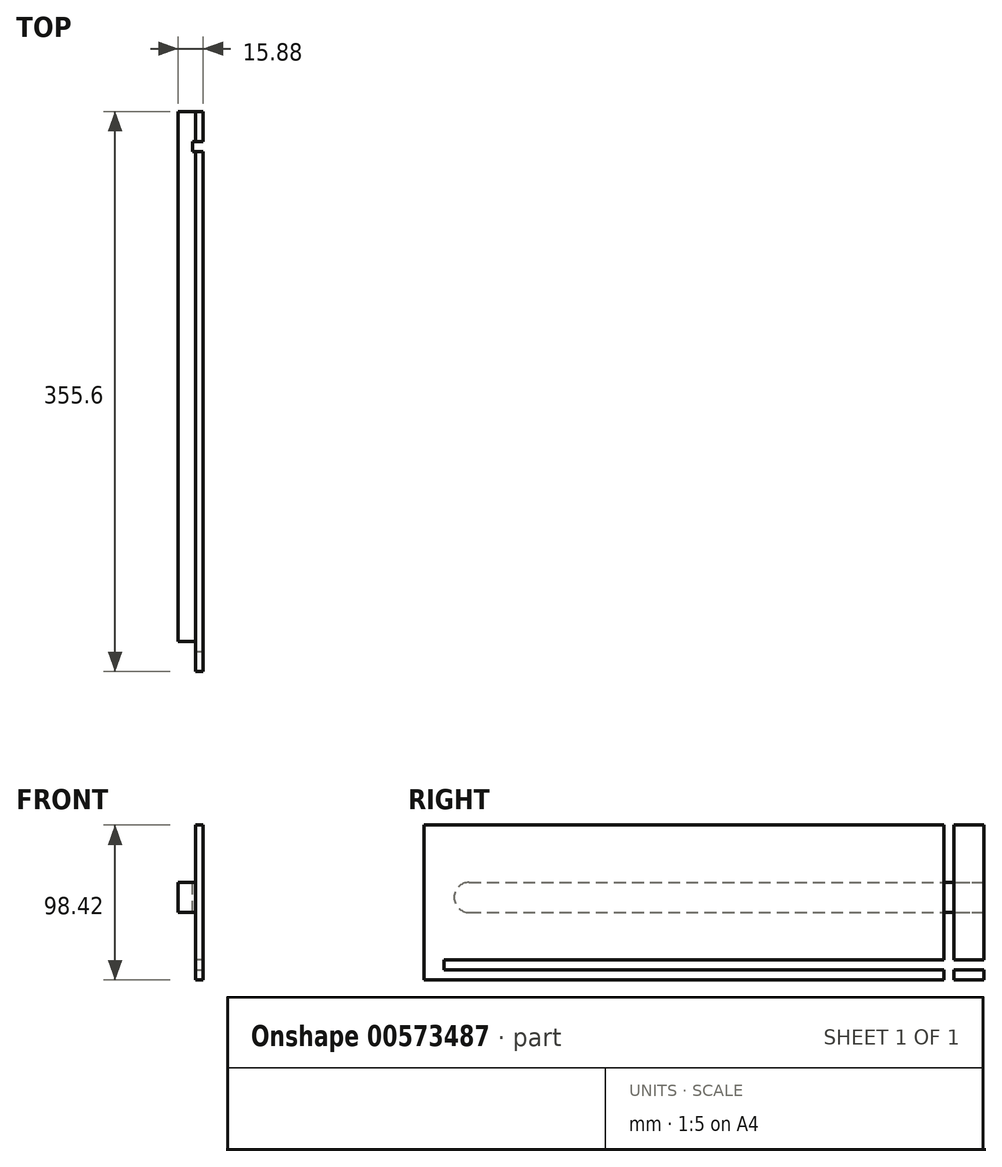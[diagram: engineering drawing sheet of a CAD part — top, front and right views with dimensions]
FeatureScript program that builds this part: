
annotation { "Feature Type Name" : "Feature", "Feature Type Description" : "" }
export const myFeature = defineFeature(function(context is Context, id is Id, definition is map)
    precondition{}
    {
        {
            var Q0;
            Q0=qCreatedBy(makeId("Right.planeOp"),FACE);
            var sketch = newSketch(context, id + "F0", { "sketchPlane" : qUnion([Q0])});
            skLineSegment(sketch, "E0.bottom", {"start": v(12.52, 0) * mm, "end": v(368.12, 0) * mm});
            skLineSegment(sketch, "E0.top", {"start": v(12.52, 98.43) * mm, "end": v(368.12, 98.43) * mm});
            skLineSegment(sketch, "E0.left", {"start": v(12.52, 0) * mm, "end": v(12.52, 98.43) * mm});
            skLineSegment(sketch, "E0.right", {"start": v(368.12, 0) * mm, "end": v(368.12, 98.43) * mm});
            skSolve(sketch);
        }
        {
            var Q0;
            Q0=makeQuery(id+"F0.imprint","IMPRINT",FACE,{"disambiguationData":[TD([[makeQuery(id+"F0.imprint","IMPRINT",EDGE,{"derivedFrom":sQuery(id+"F0.wireOp",EDGE,"E0.bottom")}),1.0]])]});
            extrude(context, id + "F1", {"entities" : qUnion([Q0]), "depth" : 15.88 * mm, "offsetDistance" : 25.4 * mm});
        }
        {
            var Q0;
            Q0=makeQuery(id+"F1.opExtrude","CAP_FACE",FACE,{"disambiguationData":[OSD([sQuery(id+"F0.wireOp",EDGE,"E0.bottom"),sQuery(id+"F0.wireOp",EDGE,"E0.top"),sQuery(id+"F0.wireOp",EDGE,"E0.left"),sQuery(id+"F0.wireOp",EDGE,"E0.right")])],"isStart":true});
            var sketch = newSketch(context, id + "F2", { "sketchPlane" : qUnion([Q0])});
            skLineSegment(sketch, "E1", {"start": v(-41.1, 52.39) * mm, "end": v(-368.12, 52.39) * mm});
            skPoint(sketch, "E1.endSnap0", {"position": v(-368.12, 49.21) * mm});
            skArc(sketch, "E2.0.startCap", {"start": v(-41.1, 61.91) * mm, "mid": v(-31.57, 52.39) * mm, "end": v(-41.1, 42.86) * mm});
            skArc(sketch, "E2.0.endCap", {"start": v(-368.12, 42.86) * mm, "mid": v(-377.65, 52.39) * mm, "end": v(-368.12, 61.91) * mm});
            skLineSegment(sketch, "E2.0.left", {"start": v(-41.1, 42.86) * mm, "end": v(-368.12, 42.86) * mm});
            skLineSegment(sketch, "E2.0.right", {"start": v(-41.1, 61.91) * mm, "end": v(-368.12, 61.91) * mm});
            skSolve(sketch);
        }
        {
            var Q0;
            Q0=makeQuery(id+"F2.imprint","IMPRINT",FACE,{"disambiguationData":[TD([[makeQuery(id+"F2.imprint","IMPRINT",EDGE,{"derivedFrom":sQuery(id+"F2.wireOp",EDGE,"E2.0.startCap")}),-1.0]])]});
            extrude(context, id + "F3", {"entities" : qUnion([Q0]), "operationType" : NewBodyOperationType.REMOVE, "oppositeDirection" : true, "depth" : 11.1 * mm, "offsetDistance" : 25.4 * mm});
        }
        {
            var Q0;
            Q0=makeQuery(id+"F1.opExtrude","CAP_FACE",FACE,{"disambiguationData":[OSD([sQuery(id+"F0.wireOp",EDGE,"E0.bottom"),sQuery(id+"F0.wireOp",EDGE,"E0.top"),sQuery(id+"F0.wireOp",EDGE,"E0.left"),sQuery(id+"F0.wireOp",EDGE,"E0.right")])],"isStart":false});
            var sketch = newSketch(context, id + "F4", { "sketchPlane" : qUnion([Q0])});
            skLineSegment(sketch, "E3.bottom", {"start": v(368.12, 6.35) * mm, "end": v(25.22, 6.35) * mm});
            skLineSegment(sketch, "E3.top", {"start": v(368.12, 12.7) * mm, "end": v(25.22, 12.7) * mm});
            skLineSegment(sketch, "E3.left", {"start": v(368.12, 6.35) * mm, "end": v(368.12, 12.7) * mm});
            skLineSegment(sketch, "E3.right", {"start": v(25.22, 6.35) * mm, "end": v(25.22, 12.7) * mm});
            skSolve(sketch);
        }
        {
            var Q0;
            Q0=makeQuery(id+"F4.imprint","IMPRINT",FACE,{"disambiguationData":[TD([[makeQuery(id+"F4.imprint","IMPRINT",EDGE,{"derivedFrom":sQuery(id+"F4.wireOp",EDGE,"E3.bottom")}),-1.0]])]});
            extrude(context, id + "F5", {"entities" : qUnion([Q0]), "operationType" : NewBodyOperationType.REMOVE, "oppositeDirection" : true, "depth" : 6.35 * mm, "offsetDistance" : 25.4 * mm});
        }
        {
            var Q0;
            Q0=makeQuery(id+"F1.opExtrude","SWEPT_FACE",FACE,{"disambiguationData":[OSD([sQuery(id+"F0.wireOp",EDGE,"E0.top")])]});
            var sketch = newSketch(context, id + "F6", { "sketchPlane" : qUnion([Q0])});
            skLineSegment(sketch, "E4.bottom", {"start": v(15.88, 349.07) * mm, "end": v(9.27, 349.07) * mm});
            skLineSegment(sketch, "E4.top", {"start": v(15.88, 342.72) * mm, "end": v(9.27, 342.72) * mm});
            skLineSegment(sketch, "E4.left", {"start": v(15.88, 349.07) * mm, "end": v(15.88, 342.72) * mm});
            skLineSegment(sketch, "E4.right", {"start": v(9.27, 349.07) * mm, "end": v(9.27, 342.72) * mm});
            skSolve(sketch);
        }
        {
            var Q0;
            Q0=makeQuery(id+"F6.imprint","IMPRINT",FACE,{"disambiguationData":[TD([[makeQuery(id+"F6.imprint","IMPRINT",EDGE,{"derivedFrom":sQuery(id+"F6.wireOp",EDGE,"E4.bottom")}),1.0]])]});
            var Q1;
            Q1=makeQuery(id+"F1.opExtrude","SWEPT_FACE",FACE,{"disambiguationData":[OSD([sQuery(id+"F0.wireOp",EDGE,"E0.bottom")])]});
            extrude(context, id + "F7", {"entities" : qUnion([Q0]), "operationType" : NewBodyOperationType.REMOVE, "endBound" : BoundingType.UP_TO_SURFACE, "oppositeDirection" : true, "depth" : 25.4 * mm, "endBoundEntityFace" : qUnion([Q1]), "offsetDistance" : 25.4 * mm});
        }
    });
